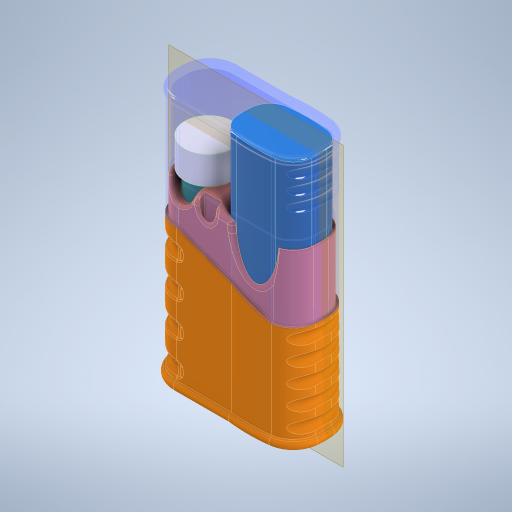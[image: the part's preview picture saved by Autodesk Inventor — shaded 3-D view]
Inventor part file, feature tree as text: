
AUTODESK INVENTOR PART (.ipt)
format: ipt  version: 2023 (Build 270158030, 158C)  size: 2,170,880 bytes
history: native  units: mm
features: sketch x21, extrude x19, fillet x16, projected_geometry x13, other x5, revolve x3, plane x1, sweep x1
ambient origin geometry x8: Origin, YZ Plane, XZ Plane, XY Plane, X Axis, Y Axis, Z Axis, Center Point
bodies: Body1 (feature_tree), Body2 (feature_tree), Body3 (feature_tree), Body4 (feature_tree)
feature tree (79):
  other  "vape"
  extrude  "Extrusion1"  Depth=8.35mm
  fillet  "Fillet1"  Radius=70.0mm
  extrude  "Extrusion2"  Depth=11.6mm TaperAngle=0.0deg
  plane  "Work Plane1"
  extrude  "Extrusion3"  Depth=45.8mm TaperAngle=0.0deg
  extrude  "Extrusion4"  Depth=22.1mm
  extrude  "Extrusion5"  Depth=1.5mm
  extrude  "Extrusion6"  Depth=1.5mm
  fillet  "Fillet2"  Radius=1.5mm
  extrude  "Extrusion8"  Depth=15.55mm
  extrude  "Extrusion20"  Depth=3.0mm
  extrude  "Extrusion21"  Depth=3.0mm
  sweep  "Sweep2"
  sketch  "Sketch26"  dims[d105=71.0mm d106=0.0mm d108=71.0mm d109=0.0mm d110=3.0mm d111=30.0deg]
  extrude  "Extrusion22"  Depth=13.0mm
  fillet  "Fillet22"  Radius=2.0mm
  fillet  "Fillet23"  Radius=10.0mm
  fillet  "Fillet24"  Radius=11.0mm
  fillet  "Fillet25"  Radius=4.0mm
  fillet  "Fillet26"  Radius=2.0mm
  fillet  "Fillet4"  Radius=2.9mm
  extrude  "Extrusion10"  Depth=2.4mm
  extrude  "Extrusion11"  Depth=7.0mm
  fillet  "Fillet10"  Radius=36.0mm
  fillet  "Fillet27"  Radius=0.25mm
  extrude  "Extrusion13"  Depth=71.0mm TaperAngle=0.0deg
  fillet  "Fillet28"  Radius=3.0mm
  sketch  "Sketch14"  dims[d50=3.0mm d51=3.0mm]
  extrude  "Extrusion14"  Depth=15.0mm TaperAngle=0.0deg
  extrude  "Extrusion23"  TaperAngle=0.0deg  [1 undecoded]
  extrude  "Extrusion24"  Depth=15.0mm
  extrude  "Extrusion15"  Depth=20.0mm
  fillet  "Fillet29"  Radius=9.0mm
  extrude  "Extrusion25"  Depth=6.0mm
  fillet  "Fillet30"  Radius=4.0mm
  other  "Work Axis1"
  revolve  "Revolution1"  [1 undecoded]
  sketch  "Sketch30"  dims[d172=15.780931mm d173=20.0mm d174=9.0mm]
  revolve  "Revolution2"  [1 undecoded]
  fillet  "Fillet31"  Radius=0.5mm
  fillet  "Fillet32"  Radius=1.0mm
  fillet  "Fillet33"  Radius=24.0mm
  extrude  "Extrusion26"  Depth=2.0mm
  sketch  "Sketch35"  dims[d178=1.0mm d179=2.0mm d180=1.0mm d181=0.5mm d182=1.0mm d183=24.0mm d184=2.0mm d185=0.5mm d186=2.0mm d187=4.0mm d188=0.5mm d189=10.0mm d190=0.0mm d191=10.0mm d192=0.0mm d193=1.5mm d194=6.0mm d195=3.65mm d196=10.0mm d197=0.0mm d198=2.5mm d199=14.0mm d200=14.0mm d201=14.0mm d203=9.0mm d205=15.0mm d206=0.0mm d207=180.0deg d208=8.0mm d209=8.0mm d210=8.0mm d211=8.0mm d212=8.0mm d213=12.5mm d214=4.0mm d215=0.0mm d216=180.0deg d217=2.5mm d218=1.5mm d219=1.5mm d220=0.5mm d221=27.75mm d222=0.0mm d223=4.0mm d224=4.0mm d225=6.0mm d226=6.0mm d227=11.5mm d228=6.0mm d229=6.0mm d230=180.0deg]
  revolve  "Revolution3"  [1 undecoded]
  sketch  "Sketch1"  dims[d4=98.5mm d5=0.0mm d9=8.35mm d22=70.0mm d23=0.0mm]
  sketch  "Sketch2"  dims[d24=20.0mm d26=11.6mm d27=0.0mm]
  other  "vape-tube"
  sketch  "Sketch3"  dims[d28=16.0mm d29=45.8mm d30=0.0mm]
  other  "storage"
  sketch  "Sketch4"  dims[d31=16.0mm d38=22.1mm]
  sketch  "Sketch5"  dims[d39=31.1mm d41=1.5mm]
  projected_geometry  "Projected Loop2"
  sketch  "Sketch6"  dims[d42=1.5mm d44=1.5mm d45=1.5mm]
  projected_geometry  "Projected Loop3"
  projected_geometry  "Projected Loop4"
  sketch  "Sketch8"  dims[d46=11.05mm d47=15.55mm]
  projected_geometry  "Projected Loop6"
  sketch  "Sketch11"  dims[d48=3.0mm d49=3.0mm]
  sketch  "Sketch15"  dims[d52=11.05mm d53=15.55mm]
  other  "vape-lid"
  sketch  "Sketch22"  dims[d54=2.0mm d55=13.0mm]
  projected_geometry  "Projected Loop13"
  sketch  "Sketch23"  dims[d56=12.5mm d57=60.0mm d58=0.0mm d59=2.0mm d60=10.0mm d61=0.0mm d62=11.0mm d66=4.0mm d67=8.726646mm d69=2.0mm d83=2.9mm]
  projected_geometry  "Projected Loop14"
  sketch  "Sketch24"  dims[d86=62.0mm d87=0.0mm d88=2.4mm]
  sketch  "Sketch25"  dims[d89=7.3mm d91=7.0mm d92=36.0mm d93=0.0mm d94=0.25mm]
  sketch  "Sketch27"  dims[d158=1.0mm d159=15.0mm d160=0.0mm]
  projected_geometry  "Projected Loop15"
  projected_geometry  "Projected Loop16"
  projected_geometry  "Projected Loop17"
  projected_geometry  "Projected Loop18"
  projected_geometry  "Projected Loop19"
  projected_geometry  "Projected Loop20"
  sketch  "Sketch28"  dims[d161=15.0mm d162=0.0mm d163=0.0mm d164=0.0mm]
  sketch  "Sketch29"  dims[d169=0.0mm d170=0.0mm d171=15.0mm]
  sketch  "Sketch33"  dims[d175=7.5mm d176=6.0mm d177=4.0mm]
  projected_geometry  "Projected Loop31"
note: 4 required parameter values undecoded (feature->parameter linkage not recoverable at this tier; creation-order binding heuristic only, values carry confidence <= 0.55)